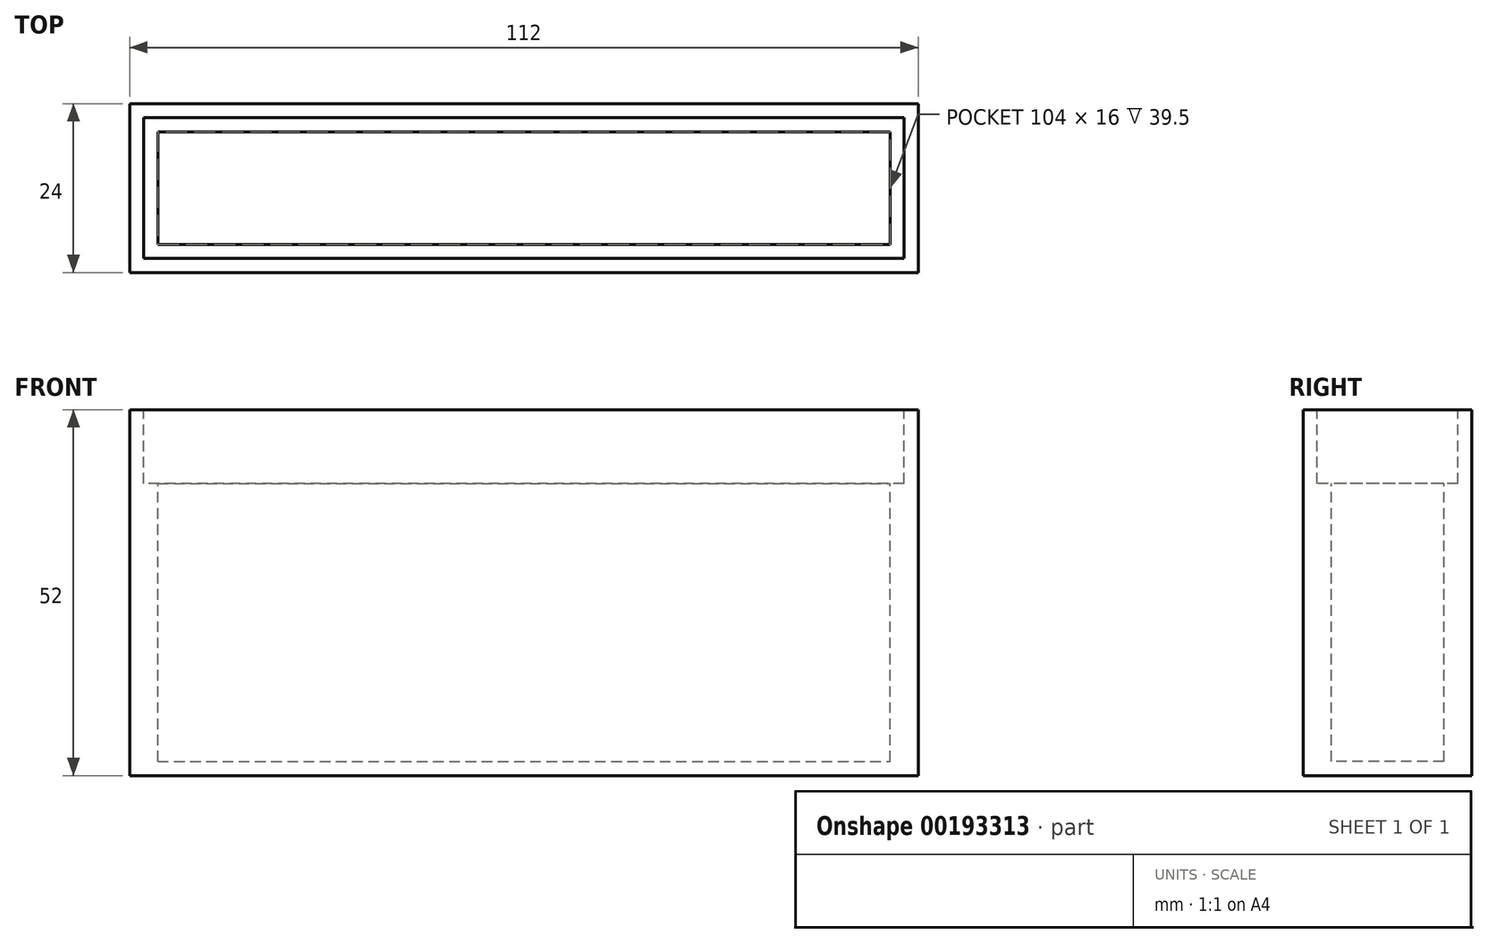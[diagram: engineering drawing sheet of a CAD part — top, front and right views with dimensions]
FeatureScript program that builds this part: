
annotation { "Feature Type Name" : "Feature", "Feature Type Description" : "" }
export const myFeature = defineFeature(function(context is Context, id is Id, definition is map)
    precondition{}
    {
        {
            var Q0;
            Q0=qCreatedBy(makeId("Top.planeOp"),FACE);
            var sketch = newSketch(context, id + "F0", { "sketchPlane" : qUnion([Q0])});
            skLineSegment(sketch, "E0.bottom", {"start": v(-28.05, 22.89) * mm, "end": v(83.95, 22.89) * mm});
            skLineSegment(sketch, "E0.top", {"start": v(-28.05, -1.11) * mm, "end": v(83.95, -1.11) * mm});
            skLineSegment(sketch, "E0.left", {"start": v(-28.05, 22.89) * mm, "end": v(-28.05, -1.11) * mm});
            skLineSegment(sketch, "E0.right", {"start": v(83.95, 22.89) * mm, "end": v(83.95, -1.11) * mm});
            skSolve(sketch);
        }
        {
            var Q0;
            Q0 = qSketchRegion(id + "F0", true);
            extrude(context, id + "F1", {"entities" : qUnion([Q0]), "depth" : 52 * mm});
        }
        {
            var Q0;
            Q0=makeQuery(id+"F1.opExtrude","CAP_FACE",FACE,{"disambiguationData":[OSD([sQuery(id+"F0.wireOp",EDGE,"E0.bottom"),sQuery(id+"F0.wireOp",EDGE,"E0.top"),sQuery(id+"F0.wireOp",EDGE,"E0.left"),sQuery(id+"F0.wireOp",EDGE,"E0.right")])],"isStart":false});
            var sketch = newSketch(context, id + "F2", { "sketchPlane" : qUnion([Q0])});
            skLineSegment(sketch, "E1.bottom", {"start": v(-24.05, 18.89) * mm, "end": v(79.95, 18.89) * mm});
            skLineSegment(sketch, "E1.top", {"start": v(-24.05, 2.89) * mm, "end": v(79.95, 2.89) * mm});
            skLineSegment(sketch, "E1.left", {"start": v(-24.05, 18.89) * mm, "end": v(-24.05, 2.89) * mm});
            skLineSegment(sketch, "E1.right", {"start": v(79.95, 18.89) * mm, "end": v(79.95, 2.89) * mm});
            skSolve(sketch);
        }
        {
            var Q0;
            Q0 = qSketchRegion(id + "F2", true);
            extrude(context, id + "F3", {"entities" : qUnion([Q0]), "operationType" : NewBodyOperationType.REMOVE, "oppositeDirection" : true, "depth" : 50 * mm});
        }
        {
            var Q0;
            Q0=makeQuery(id+"F1.opExtrude","CAP_FACE",FACE,{"disambiguationData":[OSD([sQuery(id+"F0.wireOp",EDGE,"E0.bottom"),sQuery(id+"F0.wireOp",EDGE,"E0.top"),sQuery(id+"F0.wireOp",EDGE,"E0.left"),sQuery(id+"F0.wireOp",EDGE,"E0.right")])],"isStart":false});
            var sketch = newSketch(context, id + "F4", { "sketchPlane" : qUnion([Q0])});
            skLineSegment(sketch, "E2", {"start": v(-26.05, 20.89) * mm, "end": v(-26.05, 0.89) * mm});
            skLineSegment(sketch, "E3", {"start": v(-26.05, 0.89) * mm, "end": v(81.95, 0.89) * mm});
            skLineSegment(sketch, "E4", {"start": v(81.95, 0.89) * mm, "end": v(81.95, 20.89) * mm});
            skLineSegment(sketch, "E5", {"start": v(81.95, 20.89) * mm, "end": v(-26.05, 20.89) * mm});
            skSolve(sketch);
        }
        {
            var Q0;
            Q0=makeQuery(id+"F4.imprint","IMPRINT",FACE,{"disambiguationData":[TD([[makeQuery(id+"F4.imprint","IMPRINT",EDGE,{"derivedFrom":sQuery(id+"F4.wireOp",EDGE,"E2")}),1.0]])]});
            extrude(context, id + "F5", {"entities" : qUnion([Q0]), "operationType" : NewBodyOperationType.REMOVE, "oppositeDirection" : true, "depth" : 10.5 * mm});
        }
    });
